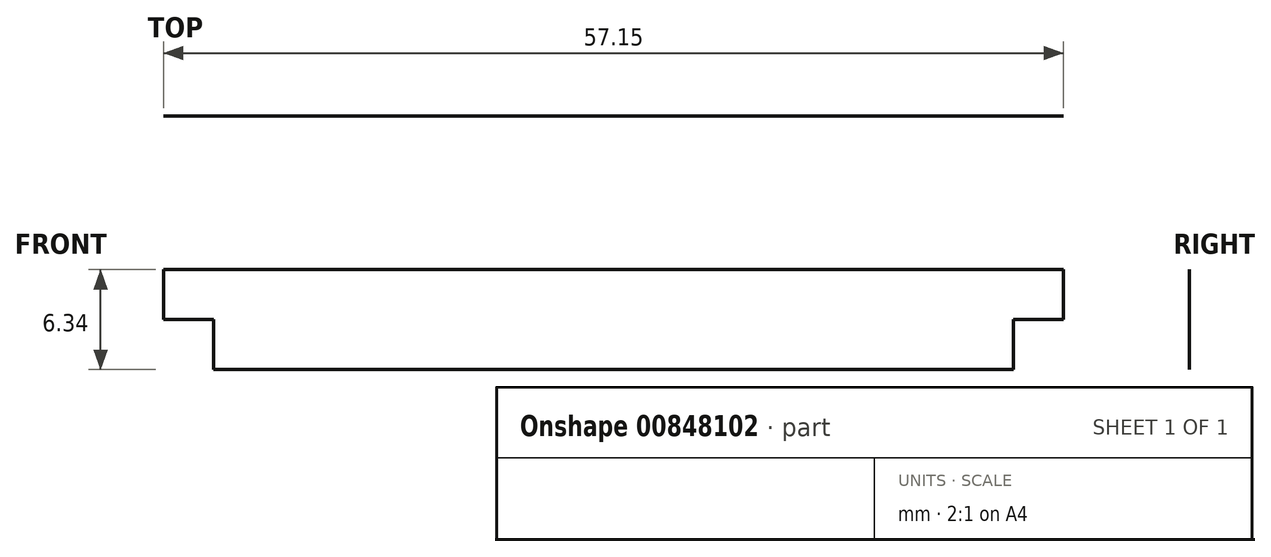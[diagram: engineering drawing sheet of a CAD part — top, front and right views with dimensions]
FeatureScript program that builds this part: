
annotation { "Feature Type Name" : "Feature", "Feature Type Description" : "" }
export const myFeature = defineFeature(function(context is Context, id is Id, definition is map)
    precondition{}
    {
        {
            var Q0;
            Q0=qCreatedBy(makeId("Front.planeOp"),FACE);
            var sketch = newSketch(context, id + "F0", { "sketchPlane" : qUnion([Q0])});
            skLineSegment(sketch, "E0", {"start": v(-24.56, 0) * mm, "end": v(-24.56, 3.18) * mm});
            skLineSegment(sketch, "E1", {"start": v(-24.56, 3.18) * mm, "end": v(32.6, 3.18) * mm});
            skLineSegment(sketch, "E2", {"start": v(32.6, 3.18) * mm, "end": v(32.6, 0) * mm});
            skLineSegment(sketch, "E3", {"start": v(32.6, 0) * mm, "end": v(29.42, 0) * mm});
            skLineSegment(sketch, "E4", {"start": v(29.42, 0) * mm, "end": v(29.42, -3.18) * mm});
            skLineSegment(sketch, "E5", {"start": v(29.42, -3.18) * mm, "end": v(-21.38, -3.18) * mm});
            skLineSegment(sketch, "E6", {"start": v(-21.38, -3.18) * mm, "end": v(-21.38, 0) * mm});
            skLineSegment(sketch, "E7", {"start": v(-21.38, 0) * mm, "end": v(-24.56, 0) * mm});
            skSolve(sketch);
        }
        {
            var Q0;
            Q0 = qSketchRegion(id + "F0", true);
            extrude(context, id + "F1", {"entities" : qUnion([Q0]), "depth" : 1 / 203.2 * mm, "offsetDistance" : 25.4 * mm});
        }
    });
